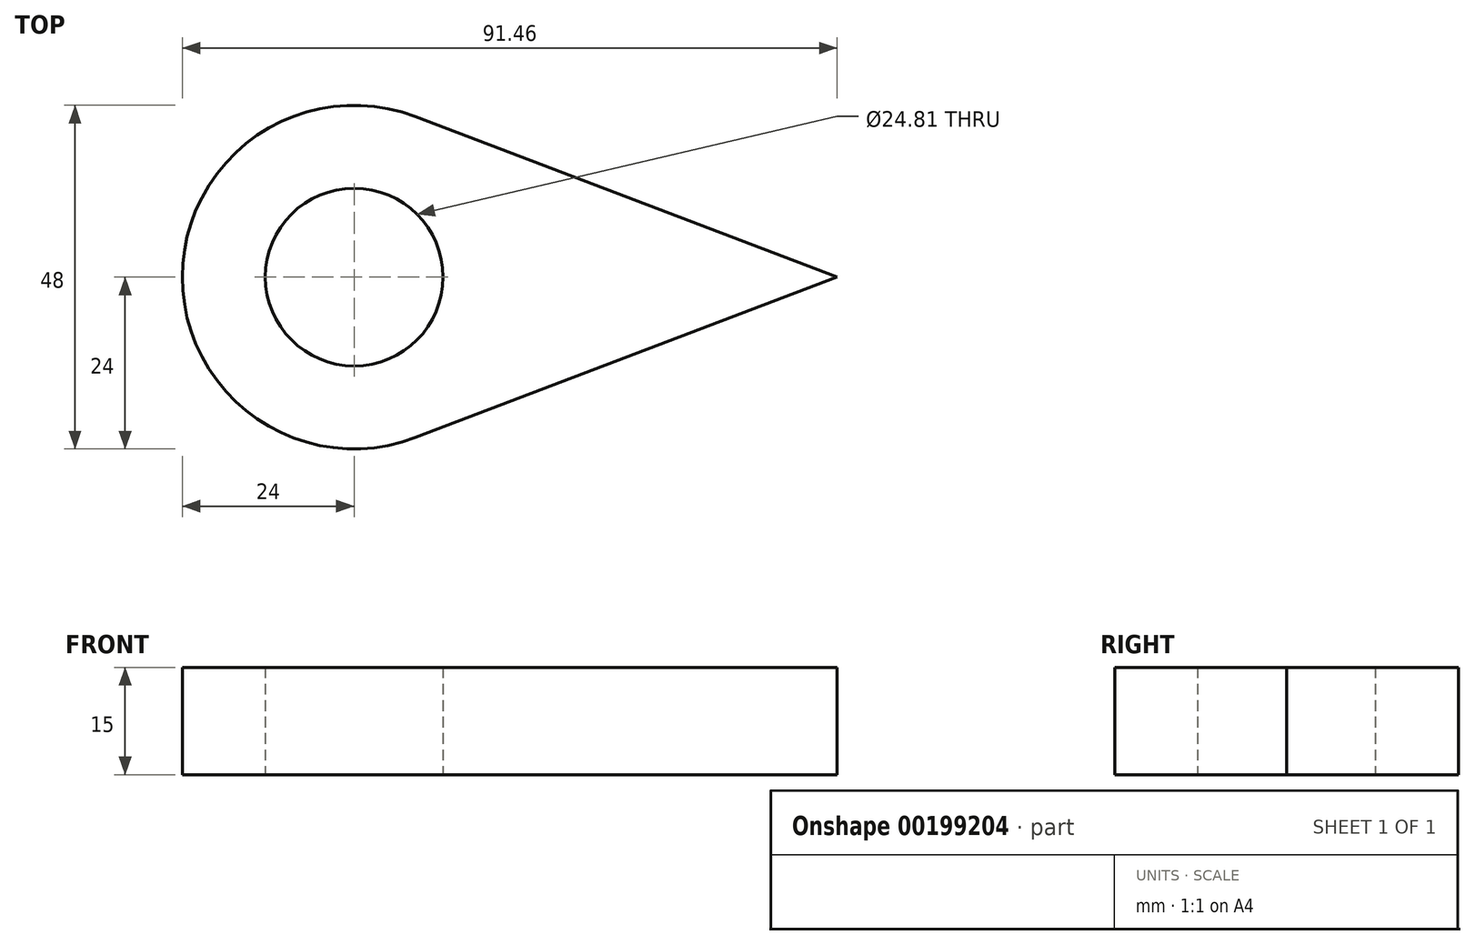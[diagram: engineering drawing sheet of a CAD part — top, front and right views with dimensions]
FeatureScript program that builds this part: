
annotation { "Feature Type Name" : "Feature", "Feature Type Description" : "" }
export const myFeature = defineFeature(function(context is Context, id is Id, definition is map)
    precondition{}
    {
        {
            var Q0;
            Q0=qCreatedBy(makeId("Top.planeOp"),FACE);
            var sketch = newSketch(context, id + "F0", { "sketchPlane" : qUnion([Q0])});
            skArc(sketch, "E0", {"start": v(8.54, 22.43) * mm, "mid": v(-24, 0) * mm, "end": v(8.54, -22.43) * mm});
            skLineSegment(sketch, "E1", {"start": v(67.46, 0) * mm, "end": v(8.54, 22.43) * mm});
            skLineSegment(sketch, "E2", {"start": v(67.46, 0) * mm, "end": v(8.54, -22.43) * mm});
            skCircle(sketch, "E3", {"center": v(0, 0) * mm, "radius": 12.4 * mm});
            skSolve(sketch);
        }
        {
            var Q0;
            Q0=makeQuery(id+"F0.imprint","IMPRINT",FACE,{"disambiguationData":[TD([[makeQuery(id+"F0.imprint","IMPRINT",EDGE,{"derivedFrom":sQuery(id+"F0.wireOp",EDGE,"E0")}),1.0]])]});
            extrude(context, id + "F1", {"entities" : qUnion([Q0]), "depth" : 15 * mm});
        }
    });
